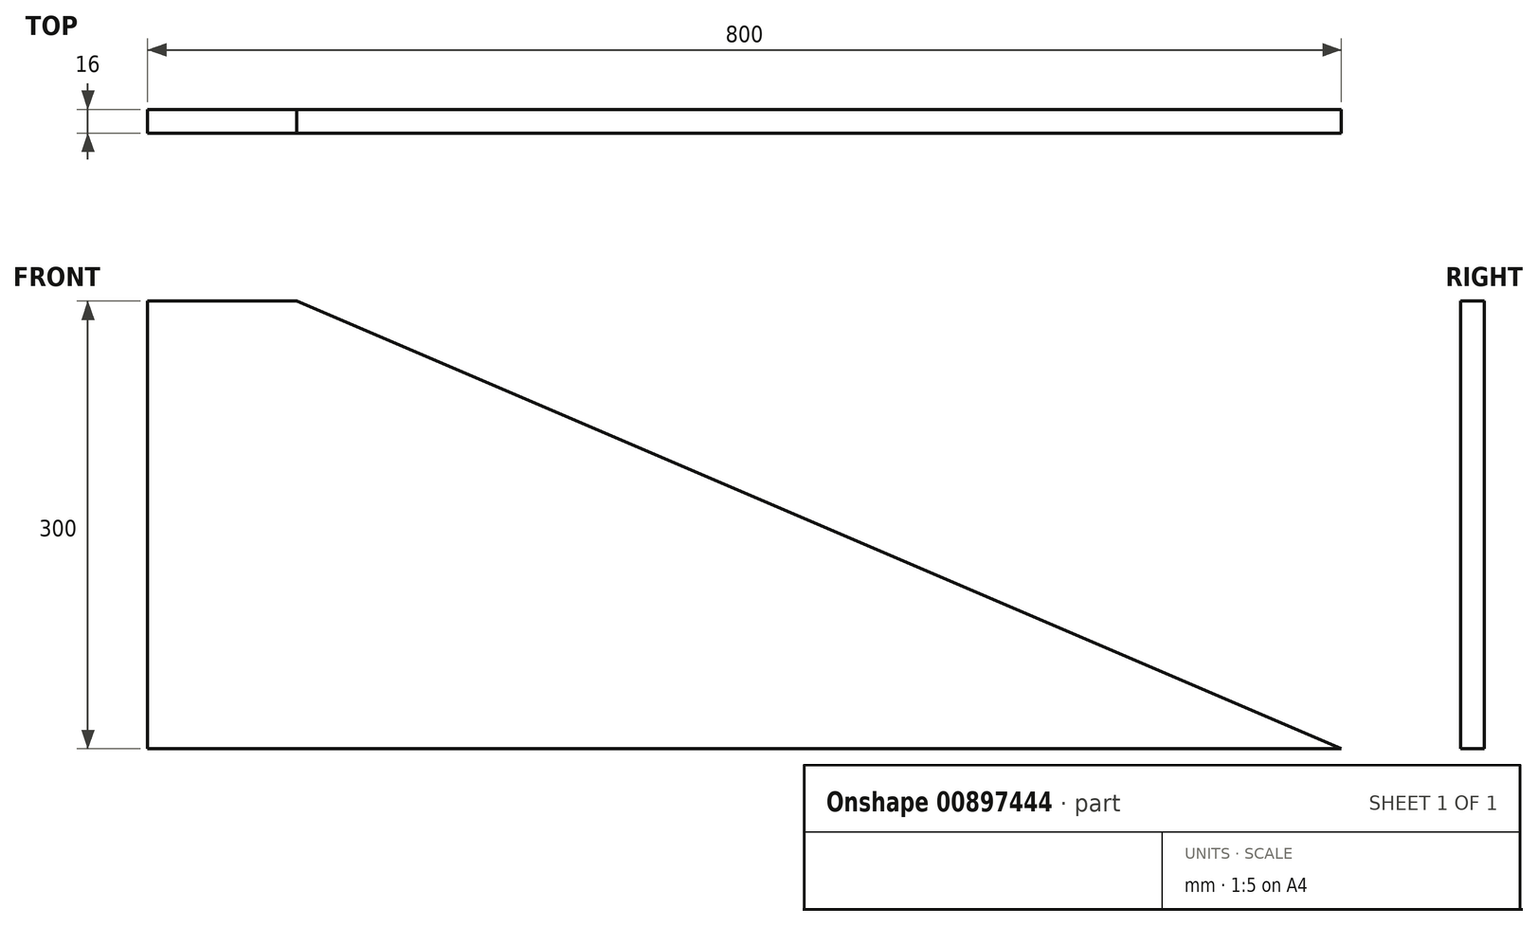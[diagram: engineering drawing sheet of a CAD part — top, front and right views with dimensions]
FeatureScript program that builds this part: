
annotation { "Feature Type Name" : "Feature", "Feature Type Description" : "" }
export const myFeature = defineFeature(function(context is Context, id is Id, definition is map)
    precondition{}
    {
        {
            var Q0;
            Q0=qCreatedBy(makeId("Front.planeOp"),FACE);
            var sketch = newSketch(context, id + "F0", { "sketchPlane" : qUnion([Q0])});
            skLineSegment(sketch, "E0.bottom", {"start": v(0, 0) * mm, "end": v(800, 0) * mm});
            skLineSegment(sketch, "E0.top", {"start": v(0, 300) * mm, "end": v(100, 300) * mm});
            skLineSegment(sketch, "E0.left", {"start": v(0, 0) * mm, "end": v(0, 300) * mm});
            skLineSegment(sketch, "E1", {"start": v(800, 0) * mm, "end": v(100, 300) * mm});
            skSolve(sketch);
        }
        {
            var Q0;
            Q0=makeQuery(id+"F0.imprint","IMPRINT",FACE,{"disambiguationData":[TD([[makeQuery(id+"F0.imprint","IMPRINT",EDGE,{"derivedFrom":sQuery(id+"F0.wireOp",EDGE,"E0.bottom")}),1.0]])]});
            extrude(context, id + "F1", {"entities" : qUnion([Q0]), "depth" : 16 * mm, "offsetDistance" : 25 * mm});
        }
    });
